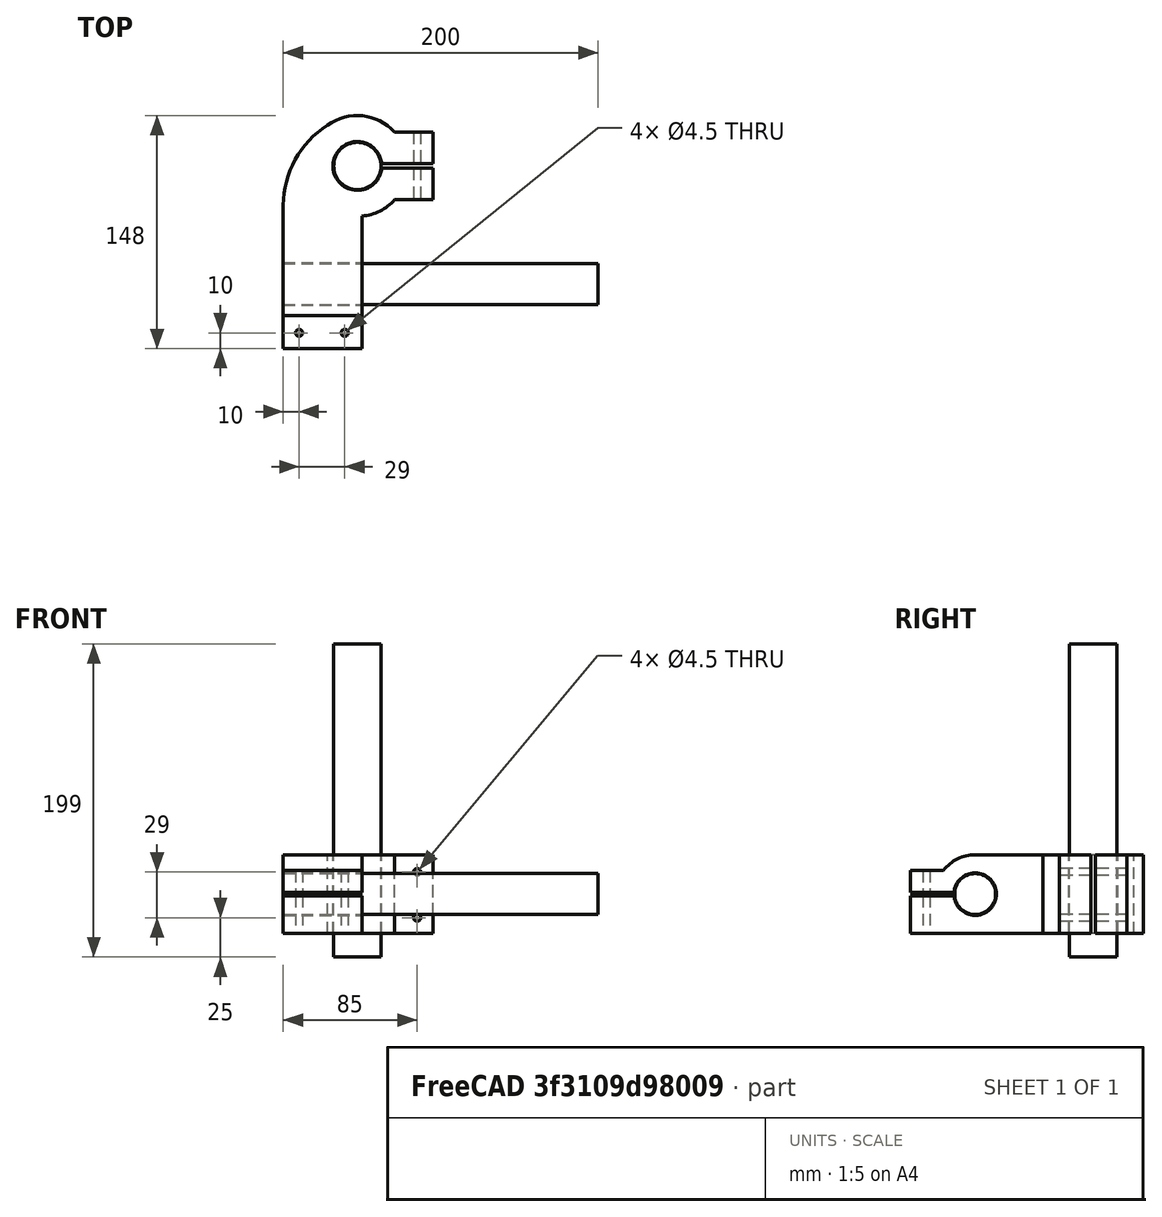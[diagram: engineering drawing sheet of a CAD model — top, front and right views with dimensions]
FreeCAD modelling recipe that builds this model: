
FCSTD DOCUMENT  (FreeCAD 0.19R24276 (Git))
Label: camMountBAck2022_02_27
License: All rights reserved
LicenseURL: http://en.wikipedia.org/wiki/All_rights_reserved
objects: Part::Cylinder×9, Part::Box×8, Part::MultiFuse×4, Part::FeaturePython×2, Part::Cut×1
note: 24 computed .brp shape members not serialized (recipe doc carries the construction recipe); baked Part::Feature solids carry a one-line shape summary decoded from their .brp

FEATURE [Part::Cylinder] Cylinder  label="Horizontal"
  Angle = 360
  AttacherType = Attacher::AttachEngine3D
  Height = 199
  Radius = 15
FEATURE [Part::Cylinder] Cylinder001  label="Vertical"
  Angle = 360
  AttacherType = Attacher::AttachEngine3D
  Height = 200
  Placement = pos=(-47,-75,40) rot=(0.57735,0.57735,0.57735;2.0944rad)
  Radius = 13
FEATURE [Part::FeaturePython] Tube  label="TubeAddons"  # WARN: FeaturePython — macro-defined, semantics opaque (R4)
  AttacherType = Attacher::AttachEngine3D
  Height = 50
  InnerRadius = 15.5
  OuterRadius = 32
  Placement = pos=(0,0,15) rot=(0,0,1;0rad)
FEATURE [Part::FeaturePython] Tube001  label="TubeAddons001"  # WARN: FeaturePython — macro-defined, semantics opaque (R4)
  AttacherType = Attacher::AttachEngine3D
  Height = 50
  InnerRadius = 13.5
  OuterRadius = 25
  Placement = pos=(-47,-75,40) rot=(0,1,0;1.5708rad)
FEATURE [Part::Box] Box  label="horCuts"
  AttacherType = Attacher::AttachEngine3D
  Height = 50
  Length = 20
  Placement = pos=(14,-1.5,15) rot=(0,0,1;0rad)
  Width = 3
FEATURE [Part::Box] Box001  label="horAdd"
  AttacherType = Attacher::AttachEngine3D
  Height = 50
  Length = 25
  Placement = pos=(23,-21.5,15) rot=(0,0,1;0rad)
  Width = 20
FEATURE [Part::Box] Box002  label="horAdd001"
  AttacherType = Attacher::AttachEngine3D
  Height = 50
  Length = 25
  Placement = pos=(23,1.5,15) rot=(0,0,1;0rad)
  Width = 20
FEATURE [Part::Box] Box003  label="VerAddons"
  AttacherType = Attacher::AttachEngine3D
  Height = 10
  Length = 50
  Placement = pos=(-47,-116,15) rot=(0,0,1;0rad)
  Width = 75
FEATURE [Part::Box] Box004  label="VerAddons001"
  AttacherType = Attacher::AttachEngine3D
  Height = 14
  Length = 50
  Placement = pos=(-47,-116,25) rot=(0,0,1;0rad)
  Width = 52
FEATURE [Part::Box] Box005  label="VerAddons002"
  AttacherType = Attacher::AttachEngine3D
  Height = 14
  Length = 50
  Placement = pos=(-47,-116,41) rot=(0,0,1;0rad)
  Width = 22
FEATURE [Part::Box] Box006  label="verCuts"
  AttacherType = Attacher::AttachEngine3D
  Height = 2
  Length = 50
  Placement = pos=(-47,-110,39) rot=(0,0,1;0rad)
  Width = 27
FEATURE [Part::Cylinder] Cylinder002  label="AddCylinder"
  Angle = 60
  AttacherType = Attacher::AttachEngine3D
  Height = 50
  Placement = pos=(13,-25,15) rot=(0,0,1;2.0944rad)
  Radius = 60
FEATURE [Part::Box] Box007  label="VerAddons003"
  AttacherType = Attacher::AttachEngine3D
  Height = 50
  Length = 50
  Placement = pos=(-47,-75,15) rot=(0,0,1;0rad)
  Width = 50
FEATURE [Part::Cylinder] Cylinder003  label="Vertical001Cuts"
  Angle = 360
  AttacherType = Attacher::AttachEngine3D
  Height = 200
  Placement = pos=(-47,-75,40) rot=(0.57735,0.57735,0.57735;2.0944rad)
  Radius = 13.5
FEATURE [Part::Cylinder] Cylinder004  label="Horizontal001Cuts"
  Angle = 360
  AttacherType = Attacher::AttachEngine3D
  Height = 199
  Radius = 15.5
FEATURE [Part::Cylinder] Cylinder005  label="m4s"
  Angle = 360
  AttacherType = Attacher::AttachEngine3D
  Height = 50
  Placement = pos=(38,22,25) rot=(1,0,0;1.5708rad)
  Radius = 2.25
FEATURE [Part::Cylinder] Cylinder006  label="m4s001"
  Angle = 360
  AttacherType = Attacher::AttachEngine3D
  Height = 50
  Placement = pos=(38,22,54) rot=(1,0,0;1.5708rad)
  Radius = 2.25
FEATURE [Part::MultiFuse] Fusion  label="m4s002"
  Placement = pos=(-62,-144,43) rot=(0.57735,0.57735,0.57735;2.0944rad)
  Shapes = -> [Cylinder006,Cylinder005]
FEATURE [Part::Cylinder] Cylinder007  label="m4s004"
  Angle = 360
  AttacherType = Attacher::AttachEngine3D
  Height = 50
  Placement = pos=(38,22,25) rot=(1,0,0;1.5708rad)
  Radius = 2.25
FEATURE [Part::Cylinder] Cylinder008  label="m4s005"
  Angle = 360
  AttacherType = Attacher::AttachEngine3D
  Height = 50
  Placement = pos=(38,22,54) rot=(1,0,0;1.5708rad)
  Radius = 2.25
FEATURE [Part::MultiFuse] Fusion001  label="m4s003"
  Shapes = -> [Cylinder008,Cylinder007]
FEATURE [Part::MultiFuse] Fusion002  label="cuts"
  Shapes = -> [Fusion001,Fusion,Cylinder004,Cylinder003,Box,Box006]
FEATURE [Part::MultiFuse] Fusion003  label="addons"
  Shapes = -> [Box007,Box001,Box002,Box003,Box004,Box005,Cylinder002,Tube,Tube001]
FEATURE [Part::Cut] Cut  label="rear"
  Base = -> Fusion003
  Tool = -> Fusion002
